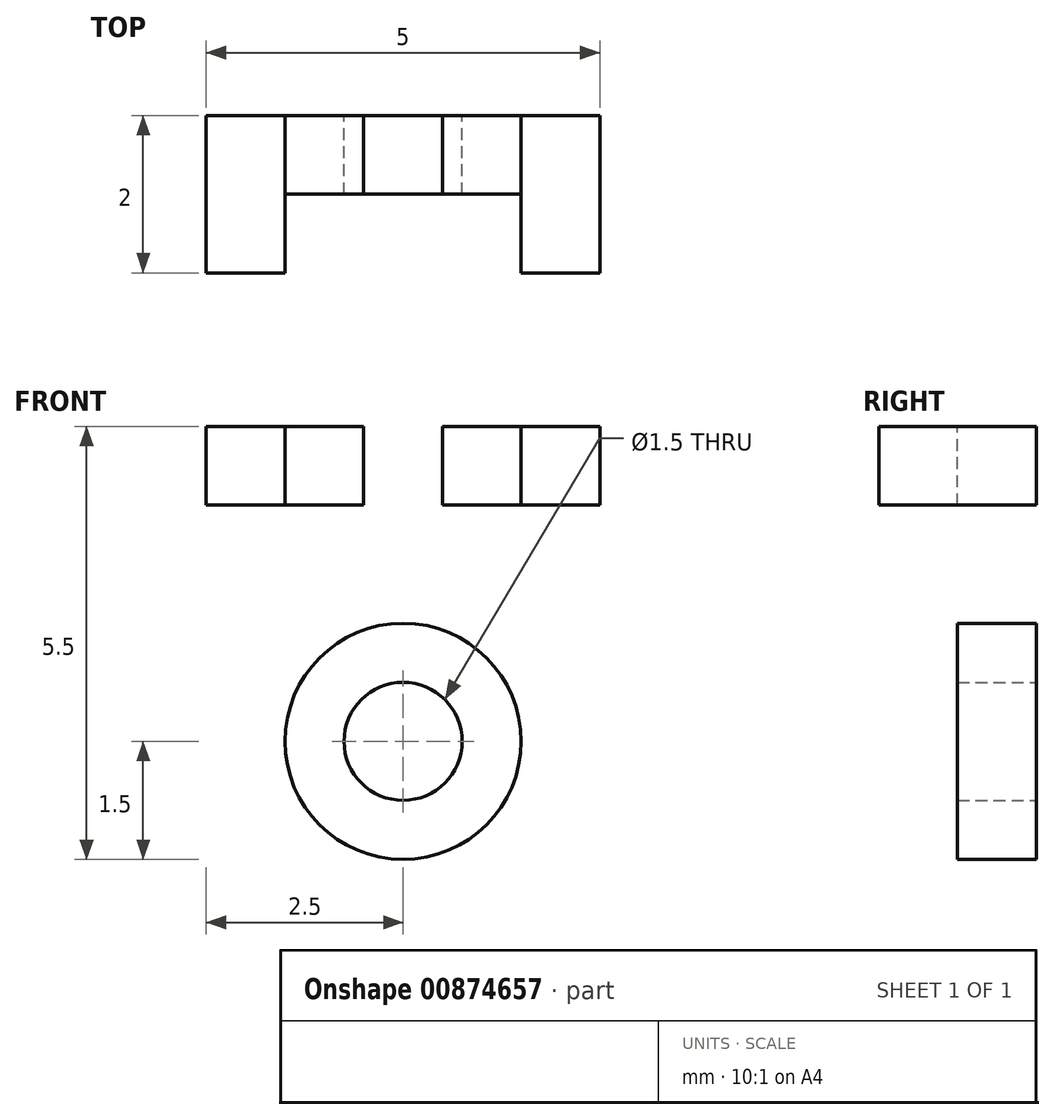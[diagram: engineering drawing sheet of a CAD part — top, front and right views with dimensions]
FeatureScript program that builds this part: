
annotation { "Feature Type Name" : "Feature", "Feature Type Description" : "" }
export const myFeature = defineFeature(function(context is Context, id is Id, definition is map)
    precondition{}
    {
        {
            var Q0;
            Q0=qCreatedBy(makeId("Front.planeOp"),FACE);
            var sketch = newSketch(context, id + "F0", { "sketchPlane" : qUnion([Q0])});
            skCircle(sketch, "E0", {"center": v(0, 0) * mm, "radius": 0.75 * mm});
            skCircle(sketch, "E1", {"center": v(0, 0) * mm, "radius": 1.5 * mm});
            skLineSegment(sketch, "E2.bottom", {"start": v(-1.5, 0) * mm, "end": v(1.5, 0) * mm});
            skLineSegment(sketch, "E2.top", {"start": v(-1.5, 4) * mm, "end": v(1.5, 4) * mm});
            skLineSegment(sketch, "E2.left", {"start": v(-1.5, 0) * mm, "end": v(-1.5, 4) * mm});
            skLineSegment(sketch, "E2.right", {"start": v(1.5, 0) * mm, "end": v(1.5, 4) * mm});
            skLineSegment(sketch, "E3.bottom", {"start": v(2.5, 3) * mm, "end": v(-2.5, 3) * mm});
            skLineSegment(sketch, "E3.top", {"start": v(2.5, 4) * mm, "end": v(-2.5, 4) * mm});
            skLineSegment(sketch, "E3.left", {"start": v(2.5, 3) * mm, "end": v(2.5, 4) * mm});
            skLineSegment(sketch, "E3.right", {"start": v(-2.5, 3) * mm, "end": v(-2.5, 4) * mm});
            skPoint(sketch, "E3.middle", {"position": v(0, 3.5) * mm});
            skLineSegment(sketch, "E4.bottom", {"start": v(0.5, 3) * mm, "end": v(-0.5, 3) * mm});
            skLineSegment(sketch, "E4.top", {"start": v(0.5, 4) * mm, "end": v(-0.5, 4) * mm});
            skLineSegment(sketch, "E4.left", {"start": v(0.5, 3) * mm, "end": v(0.5, 4) * mm});
            skLineSegment(sketch, "E4.right", {"start": v(-0.5, 3) * mm, "end": v(-0.5, 4) * mm});
            skSolve(sketch);
        }
        {
            var Q0;
            {var subQ5=sQuery(id+"F0.wireOp",EDGE,"E3.right");Q0=makeQuery(id+"F0.imprint","IMPRINT",FACE,{"disambiguationData":[TD([[makeQuery(id+"F0.imprint","IMPRINT",EDGE,{"derivedFrom":subQ5}),-1.0]])]});}
            var Q1;
            Q1=makeQuery(id+"F0.imprint","IMPRINT",FACE,{"disambiguationData":[TD([[makeQuery(id+"F0.imprint","IMPRINT",EDGE,{"derivedFrom":sQuery(id+"F0.wireOp",EDGE,"E4.bottom")}),-1.0]])]});
            var Q2;
            {var subQ5=sQuery(id+"F0.wireOp",EDGE,"E3.left");Q2=makeQuery(id+"F0.imprint","IMPRINT",FACE,{"disambiguationData":[TD([[makeQuery(id+"F0.imprint","IMPRINT",EDGE,{"derivedFrom":subQ5}),1.0]])]});}
            extrude(context, id + "F1", {"entities" : qUnion([Q0, Q1, Q2]), "depth" : 2 * mm, "offsetDistance" : 25 * mm});
        }
        {
            var Q0;
            {var subQ5=sQuery(id+"F0.wireOp",EDGE,"E4.right");Q0=makeQuery(id+"F0.imprint","IMPRINT",FACE,{"disambiguationData":[TD([[makeQuery(id+"F0.imprint","IMPRINT",EDGE,{"derivedFrom":subQ5}),1.0]])]});}
            var Q1;
            {var subQ5=sQuery(id+"F0.wireOp",EDGE,"E4.left");Q1=makeQuery(id+"F0.imprint","IMPRINT",FACE,{"disambiguationData":[TD([[makeQuery(id+"F0.imprint","IMPRINT",EDGE,{"derivedFrom":subQ5}),-1.0]])]});}
            var Q2;
            {var subQ6=sQuery(id+"F0.wireOp",EDGE,"E4.bottom");Q2=makeQuery(id+"F0.imprint","IMPRINT",FACE,{"disambiguationData":[TD([[makeQuery(id+"F0.imprint","IMPRINT",EDGE,{"derivedFrom":subQ6}),1.0]])]});}
            var Q3;
            {var subQ0=sQuery(id+"F0.wireOp",EDGE,"E2.bottom");var subQ1=sQuery(id+"F0.wireOp",EDGE,"E0");var subQ2=makeQuery(id+"F0.imprint","INTERSECT",VERTEX,{"disambiguationData":[OD(0.0)],"derivedFrom":[subQ1,subQ0]});Q3=makeQuery(id+"F0.imprint","IMPRINT",FACE,{"disambiguationData":[TD([[makeQuery(id+"F0.imprint","IMPRINT",EDGE,{"disambiguationData":[TD([[subQ2,1.0]])],"derivedFrom":subQ1}),-1.0]])]});}
            var Q4;
            {var subQ0=sQuery(id+"F0.wireOp",EDGE,"E2.bottom");var subQ1=sQuery(id+"F0.wireOp",EDGE,"E0");var subQ2=makeQuery(id+"F0.imprint","INTERSECT",VERTEX,{"disambiguationData":[OD(0.0)],"derivedFrom":[subQ1,subQ0]});Q4=makeQuery(id+"F0.imprint","IMPRINT",FACE,{"disambiguationData":[TD([[makeQuery(id+"F0.imprint","IMPRINT",EDGE,{"disambiguationData":[TD([[subQ2,-1.0]])],"derivedFrom":subQ1}),-1.0]])]});}
            extrude(context, id + "F2", {"entities" : qUnion([Q0, Q1, Q2, Q3, Q4]), "depth" : 1 * mm, "offsetDistance" : 25 * mm});
        }
    });
